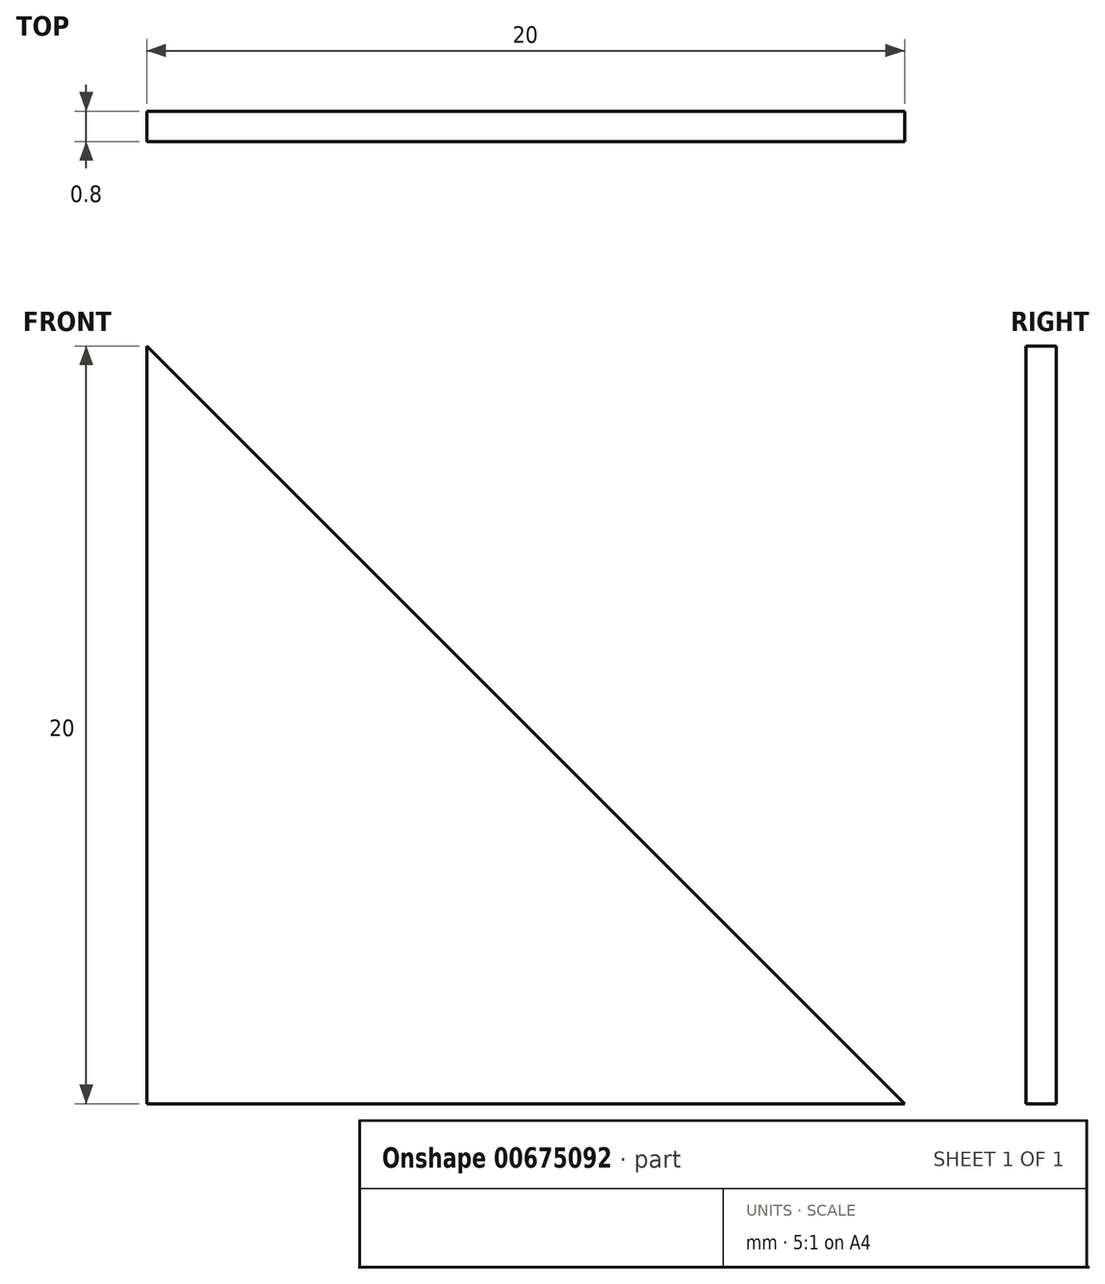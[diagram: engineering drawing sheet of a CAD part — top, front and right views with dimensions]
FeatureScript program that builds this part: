
annotation { "Feature Type Name" : "Feature", "Feature Type Description" : "" }
export const myFeature = defineFeature(function(context is Context, id is Id, definition is map)
    precondition{}
    {
        {
            var Q0;
            Q0=qCreatedBy(makeId("Front.planeOp"),FACE);
            var sketch = newSketch(context, id + "F0", { "sketchPlane" : qUnion([Q0])});
            skLineSegment(sketch, "E0.bottom", {"start": v(0, 0) * mm, "end": v(20, 0) * mm});
            skLineSegment(sketch, "E0.top", {"start": v(0, 20) * mm, "end": v(20, 20) * mm});
            skLineSegment(sketch, "E0.left", {"start": v(0, 0) * mm, "end": v(0, 20) * mm});
            skLineSegment(sketch, "E0.right", {"start": v(20, 0) * mm, "end": v(20, 20) * mm});
            skLineSegment(sketch, "E1", {"start": v(0, 20) * mm, "end": v(20, 0) * mm});
            skSolve(sketch);
        }
        {
            var Q0;
            Q0=makeQuery(id+"F0.imprint","IMPRINT",FACE,{"disambiguationData":[TD([[makeQuery(id+"F0.imprint","IMPRINT",EDGE,{"derivedFrom":sQuery(id+"F0.wireOp",EDGE,"E0.bottom")}),1.0]])]});
            extrude(context, id + "F1", {"entities" : qUnion([Q0]), "endBound" : BoundingType.SYMMETRIC, "depth" : 0.8 * mm, "offsetDistance" : 25 * mm});
        }
    });
